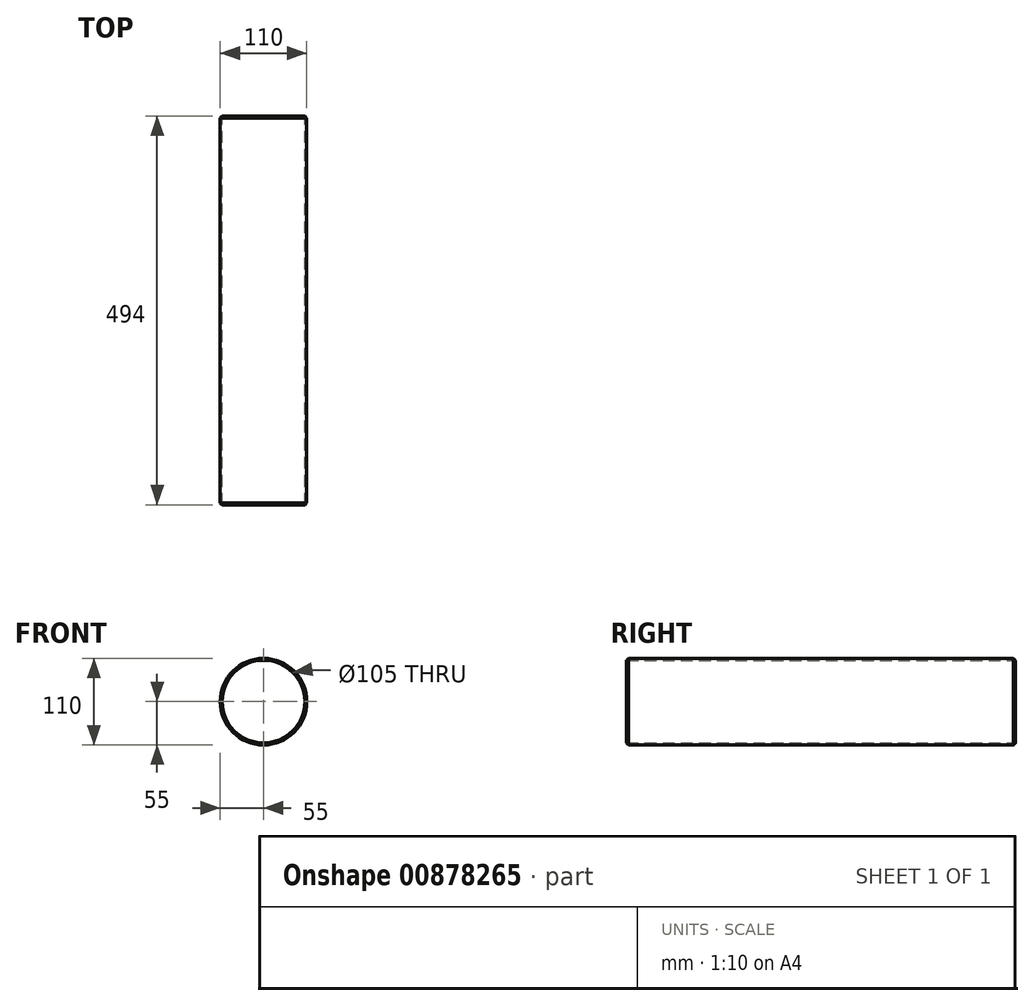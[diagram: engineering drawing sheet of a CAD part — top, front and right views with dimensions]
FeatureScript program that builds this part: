
annotation { "Feature Type Name" : "Feature", "Feature Type Description" : "" }
export const myFeature = defineFeature(function(context is Context, id is Id, definition is map)
    precondition{}
    {
        {
            var Q0;
            Q0=qCreatedBy(makeId("Front.planeOp"),FACE);
            var sketch = newSketch(context, id + "F0", { "sketchPlane" : qUnion([Q0])});
            skCircle(sketch, "E0", {"center": v(0, 0) * mm, "radius": 52.5 * mm});
            skCircle(sketch, "E1", {"center": v(0, 0) * mm, "radius": 55 * mm});
            skSolve(sketch);
        }
        {
            var Q0;
            Q0=makeQuery(id+"F0.imprint","IMPRINT",FACE,{"disambiguationData":[TD([[makeQuery(id+"F0.imprint","IMPRINT",EDGE,{"derivedFrom":sQuery(id+"F0.wireOp",EDGE,"E0")}),-1.0]])]});
            extrude(context, id + "F1", {"entities" : qUnion([Q0]), "depth" : 500 * mm, "offsetDistance" : 25 * mm});
        }
        {
            var Q0;
            Q0=qCreatedBy(makeId("Right.planeOp"),FACE);
            var sketch = newSketch(context, id + "F2", { "sketchPlane" : qUnion([Q0])});
            skLineSegment(sketch, "E2", {"start": v(0, 55) * mm, "end": v(0, 49.5) * mm});
            skLineSegment(sketch, "E3", {"start": v(0, 49.5) * mm, "end": v(-5.5, 55) * mm});
            skLineSegment(sketch, "E4", {"start": v(-5.5, 55) * mm, "end": v(0, 55) * mm});
            skSolve(sketch);
        }
        {
            var Q0;
            Q0=makeQuery(id+"F2.imprint","IMPRINT",FACE,{"disambiguationData":[TD([[makeQuery(id+"F2.imprint","IMPRINT",EDGE,{"derivedFrom":sQuery(id+"F2.wireOp",EDGE,"E2")}),-1.0]])]});
            var Q1;
            Q1=makeQuery(id+"F1.opExtrude","CAP_EDGE",EDGE,{"disambiguationData":[OSD([sQuery(id+"F0.wireOp",EDGE,"E1")])],"isStart":true});
            revolve(context, id + "F3", {"operationType" : NewBodyOperationType.REMOVE, "surfaceOperationType" : NewSurfaceOperationType.NEW, "entities" : qUnion([Q0]), "axis" : qUnion([Q1]), "revolveType" : RevolveType.FULL, "oppositeDirection" : true});
        }
        {
            var Q0;
            Q0=qCreatedBy(makeId("Right.planeOp"),FACE);
            var sketch = newSketch(context, id + "F4", { "sketchPlane" : qUnion([Q0])});
            skLineSegment(sketch, "E5", {"start": v(-494.5, 55) * mm, "end": v(-500, 49.5) * mm});
            skLineSegment(sketch, "E6", {"start": v(-500, 49.5) * mm, "end": v(-500, 55) * mm});
            skLineSegment(sketch, "E7", {"start": v(-500, 55) * mm, "end": v(-494.5, 55) * mm});
            skSolve(sketch);
        }
        {
            var Q0;
            Q0=makeQuery(id+"F4.imprint","IMPRINT",FACE,{"disambiguationData":[TD([[makeQuery(id+"F4.imprint","IMPRINT",EDGE,{"derivedFrom":sQuery(id+"F4.wireOp",EDGE,"E5")}),-1.0]])]});
            var Q1;
            Q1=makeQuery(id+"F1.opExtrude","CAP_EDGE",EDGE,{"disambiguationData":[OSD([sQuery(id+"F0.wireOp",EDGE,"E1")])],"isStart":false});
            revolve(context, id + "F5", {"operationType" : NewBodyOperationType.REMOVE, "surfaceOperationType" : NewSurfaceOperationType.NEW, "entities" : qUnion([Q0]), "axis" : qUnion([Q1]), "revolveType" : RevolveType.FULL, "oppositeDirection" : true});
        }
    });
